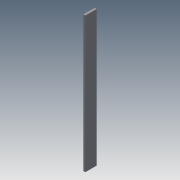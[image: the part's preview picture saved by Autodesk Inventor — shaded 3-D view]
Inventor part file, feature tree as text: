
AUTODESK INVENTOR PART (.ipt)
format: ipt  version: 2015 (Build 190159000, 159)  size: 67,072 bytes
history: native  units: mm
features: extrude x1, sketch x1
ambient origin geometry x8: Origin, YZ Plane, XZ Plane, XY Plane, X Axis, Y Axis, Z Axis, Center Point
bodies: Solid1 (feature_tree)
feature tree (2):
  extrude  "Extrusion1"  Depth=600.0mm
  sketch  "Sketch1"  dims[d0=50.0mm d1=600.0mm d2=9.0mm d3=0.0mm]
